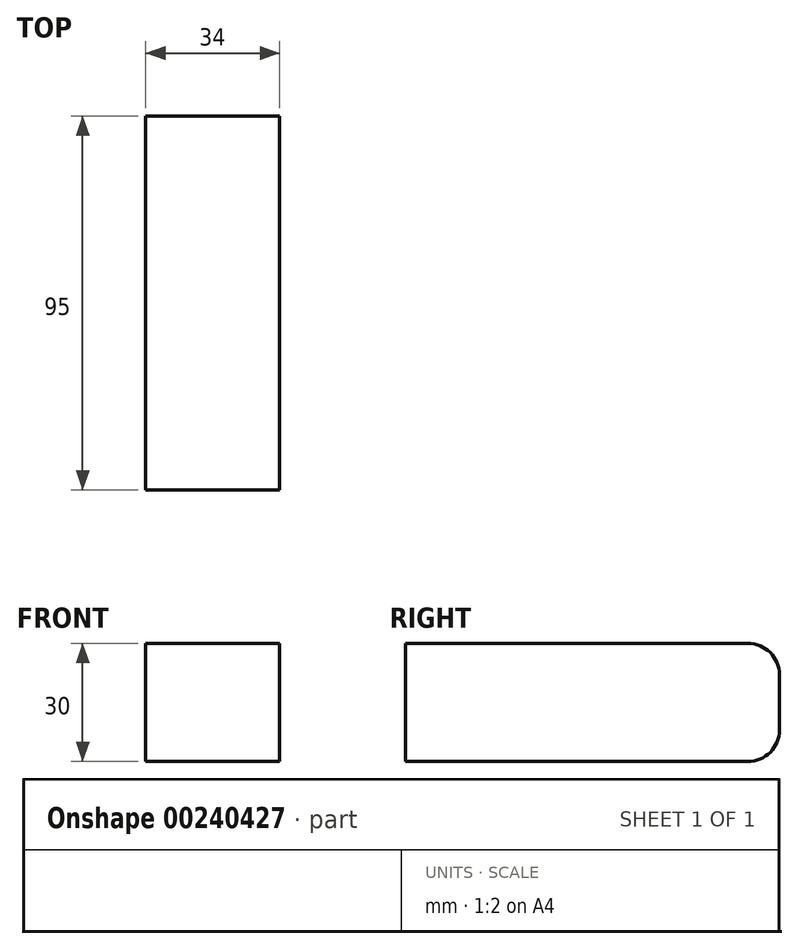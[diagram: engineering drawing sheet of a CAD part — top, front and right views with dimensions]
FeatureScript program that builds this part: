
annotation { "Feature Type Name" : "Feature", "Feature Type Description" : "" }
export const myFeature = defineFeature(function(context is Context, id is Id, definition is map)
    precondition{}
    {
        {
            var Q0;
            Q0=qCreatedBy(makeId("Right.planeOp"),FACE);
            var sketch = newSketch(context, id + "F0", { "sketchPlane" : qUnion([Q0])});
            skLineSegment(sketch, "E0.bottom", {"start": v(-35.06, 16.54) * mm, "end": v(59.94, 16.54) * mm});
            skLineSegment(sketch, "E0.top", {"start": v(-35.06, -13.46) * mm, "end": v(59.94, -13.46) * mm});
            skLineSegment(sketch, "E0.left", {"start": v(-35.06, 16.54) * mm, "end": v(-35.06, -13.46) * mm});
            skLineSegment(sketch, "E0.right", {"start": v(59.94, 16.54) * mm, "end": v(59.94, -13.46) * mm});
            skSolve(sketch);
        }
        {
            var Q0;
            Q0=makeQuery(id+"F0.imprint","IMPRINT",FACE,{"disambiguationData":[TD([[makeQuery(id+"F0.imprint","IMPRINT",EDGE,{"derivedFrom":sQuery(id+"F0.wireOp",EDGE,"E0.bottom")}),-1.0]])]});
            extrude(context, id + "F1", {"entities" : qUnion([Q0]), "depth" : 34 * mm});
        }
        {
            var Q0;
            Q0=makeQuery(id+"F1.opExtrude","SWEPT_EDGE",EDGE,{"disambiguationData":[OSD([sQuery(id+"F0.wireOp",EDGE,"E0.bottom"),sQuery(id+"F0.wireOp",EDGE,"E0.right")])]});
            var Q1;
            Q1=makeQuery(id+"F1.opExtrude","SWEPT_EDGE",EDGE,{"disambiguationData":[OSD([sQuery(id+"F0.wireOp",EDGE,"E0.top"),sQuery(id+"F0.wireOp",EDGE,"E0.right")])]});
            fillet(context, id + "F2", {"entities" : qUnion([Q0, Q1]), "radius" : 8 * mm, "tangentPropagation" : true, "allowEdgeOverflow" : false});
        }
    });
